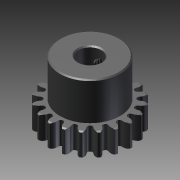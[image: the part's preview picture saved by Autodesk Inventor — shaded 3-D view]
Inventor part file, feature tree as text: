
AUTODESK INVENTOR PART (.ipt)
format: ipt  version: 2011 SP1 (Build 150282100, 282)  size: 634,880 bytes
history: native  units: mm
features: other x21, revolve x4, sketch x4, extrude x1, hole x1, thread x1
ambient origin geometry x8: Origin, YZ Plane, XZ Plane, XY Plane, X Axis, Y Axis, Z Axis, Center Point
bodies: Solid1 (feature_tree)
feature tree (32):
  revolve  "Revolution1"  [1 undecoded]
  extrude  "Extrusion1"  TaperAngle=360.0deg  [1 undecoded]
  hole  "Hole1"  [1 undecoded]
  revolve  "Revolution2"  [1 undecoded]
  revolve  "Revolution3"  [1 undecoded]
  revolve  "Revolution4"  [1 undecoded]
  thread  "Thread1"  [1 undecoded]
  other  "b_XY"
  other  "b_YZ"
  other  "b_ZX"
  other  "b_X"
  other  "b_Y"
  other  "b_Z"
  other  "b_Center"
  other  "screw_XY"
  other  "screw_YZ"
  other  "screw_ZX"
  other  "screw_X"
  other  "screw_Y"
  other  "screw_Z"
  other  "screw_Center"
  other  "turn_around_XY"
  other  "turn_around_YZ"
  other  "turn_around_ZX"
  other  "turn_around_X"
  other  "turn_around_Y"
  other  "turn_around_Z"
  other  "turn_around_Center"
  sketch  "Sketch_2"  dims[d0=360.0deg d1=6.0mm d2=0.0mm]
  sketch  "Sketch_3"  dims[d3=6.0mm d4=6.0mm d5=4.0mm d6=2.0mm d7=90.0deg d8=16.0mm d9=0.0mm d10=360.0deg]
  sketch  "Sketch3"  dims[d11=360.0deg d12=360.0deg]
  sketch  "Sketch_4"  dims[d13=4.621mm d14=0.0mm d15=0.0mm]
note: 7 required parameter values undecoded (feature->parameter linkage not recoverable at this tier; creation-order binding heuristic only, values carry confidence <= 0.55)